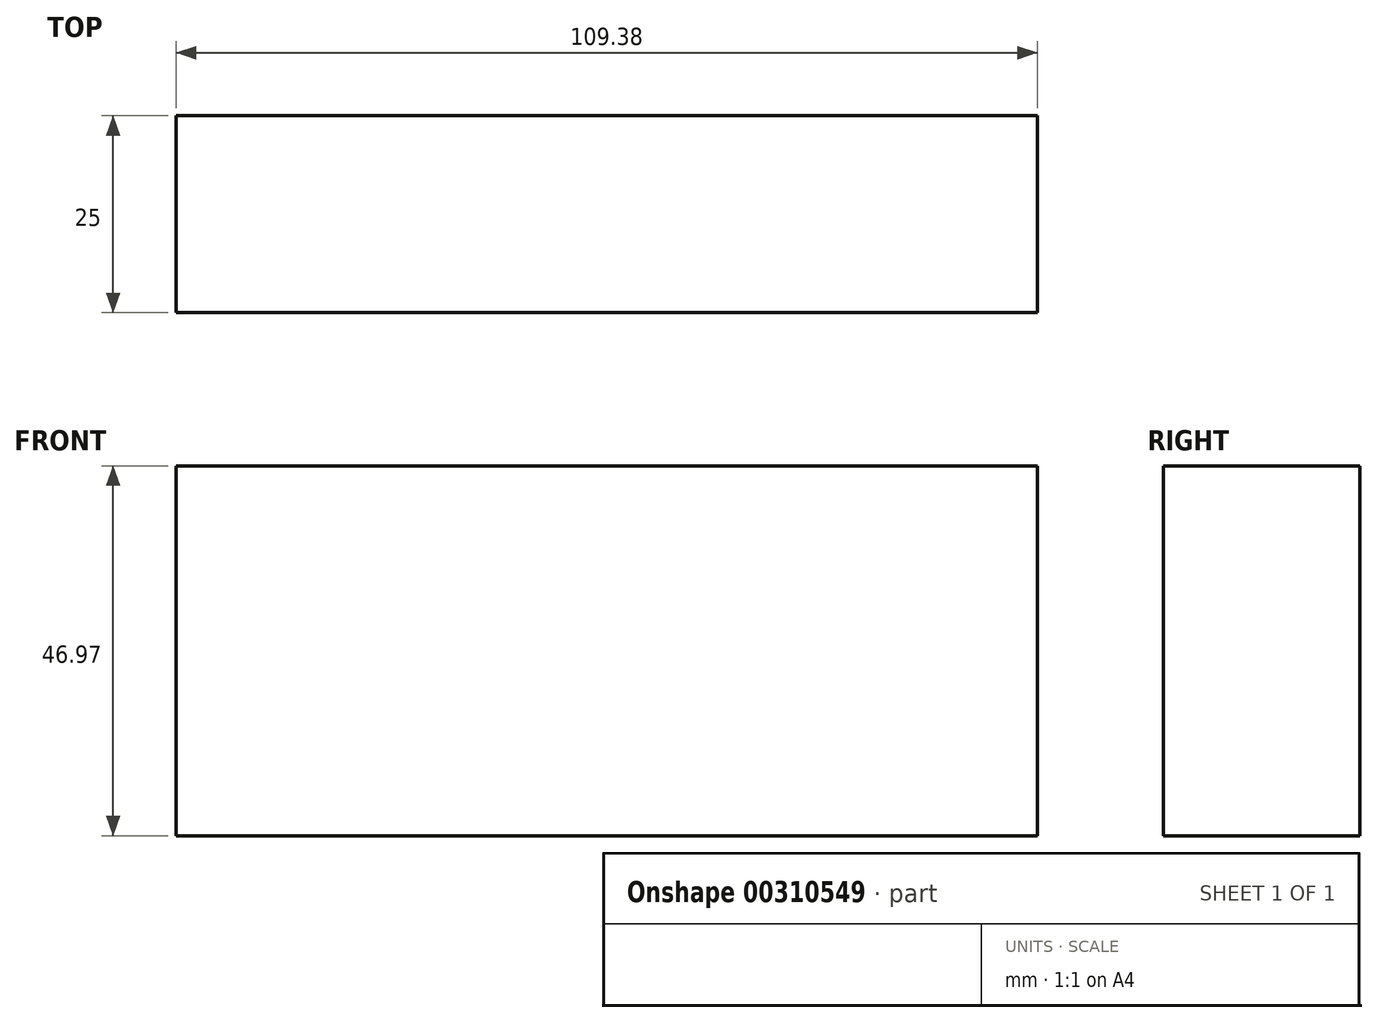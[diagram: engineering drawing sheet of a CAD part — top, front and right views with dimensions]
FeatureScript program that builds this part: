
annotation { "Feature Type Name" : "Feature", "Feature Type Description" : "" }
export const myFeature = defineFeature(function(context is Context, id is Id, definition is map)
    precondition{}
    {
        {
            var Q0;
            Q0=qCreatedBy(makeId("Front.planeOp"),FACE);
            var sketch = newSketch(context, id + "F0", { "sketchPlane" : qUnion([Q0])});
            skLineSegment(sketch, "E0.bottom", {"start": v(-106.62, 41.92) * mm, "end": v(2.76, 41.92) * mm});
            skLineSegment(sketch, "E0.top", {"start": v(-106.62, -5.05) * mm, "end": v(2.76, -5.05) * mm});
            skLineSegment(sketch, "E0.left", {"start": v(-106.62, 41.92) * mm, "end": v(-106.62, -5.05) * mm});
            skLineSegment(sketch, "E0.right", {"start": v(2.76, 41.92) * mm, "end": v(2.76, -5.05) * mm});
            skSolve(sketch);
        }
        {
            var Q0;
            Q0=qSketchRegion(id+"F0",true);
            extrude(context, id + "F1", {"entities" : qUnion([Q0]), "depth" : 25 * mm});
        }
    });
